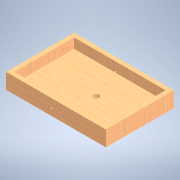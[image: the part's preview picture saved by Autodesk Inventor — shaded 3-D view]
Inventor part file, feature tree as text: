
AUTODESK INVENTOR PART (.ipt)
format: ipt  version: 2020 (Build 240168000, 168)  size: 143,872 bytes
history: native  units: in
note: dims shown in document units (in); Inventor stores cm internally (conversion verified against a paired STEP export)
features: extrude x4, sketch x4
ambient origin geometry x8: Origin, YZ Plane, XZ Plane, XY Plane, X Axis, Y Axis, Z Axis, Center Point
bodies: Solid1 (feature_tree)
feature tree (8):
  extrude  "Extrusion1"  Depth=13.9764in TaperAngle=0.0deg
  extrude  "Extrusion3"  TaperAngle=0.0deg  [1 undecoded]
  extrude  "Extrusion4"  Depth=1.378in TaperAngle=0.0deg
  extrude  "Extrusion5"  Depth=13.9764in
  sketch  "Sketch1"  dims[d0=2.1654in d1=9.5276in d2=13.9764in d3=0.0in]
  sketch  "Sketch3"  dims[d8=0.7874in d9=0.0in d10=0.0in]
  sketch  "Sketch4"  dims[d11=0.5906in d12=0.5906in d13=1.378in d14=0.0in]
  sketch  "Sketch5"  dims[d15=0.2362in d16=0.0in d17=0.0in d18=6.3544in d19=13.9764in d20=0.9092in]
note: 1 required parameter value undecoded (feature->parameter linkage not recoverable at this tier; creation-order binding heuristic only, values carry confidence <= 0.55)
